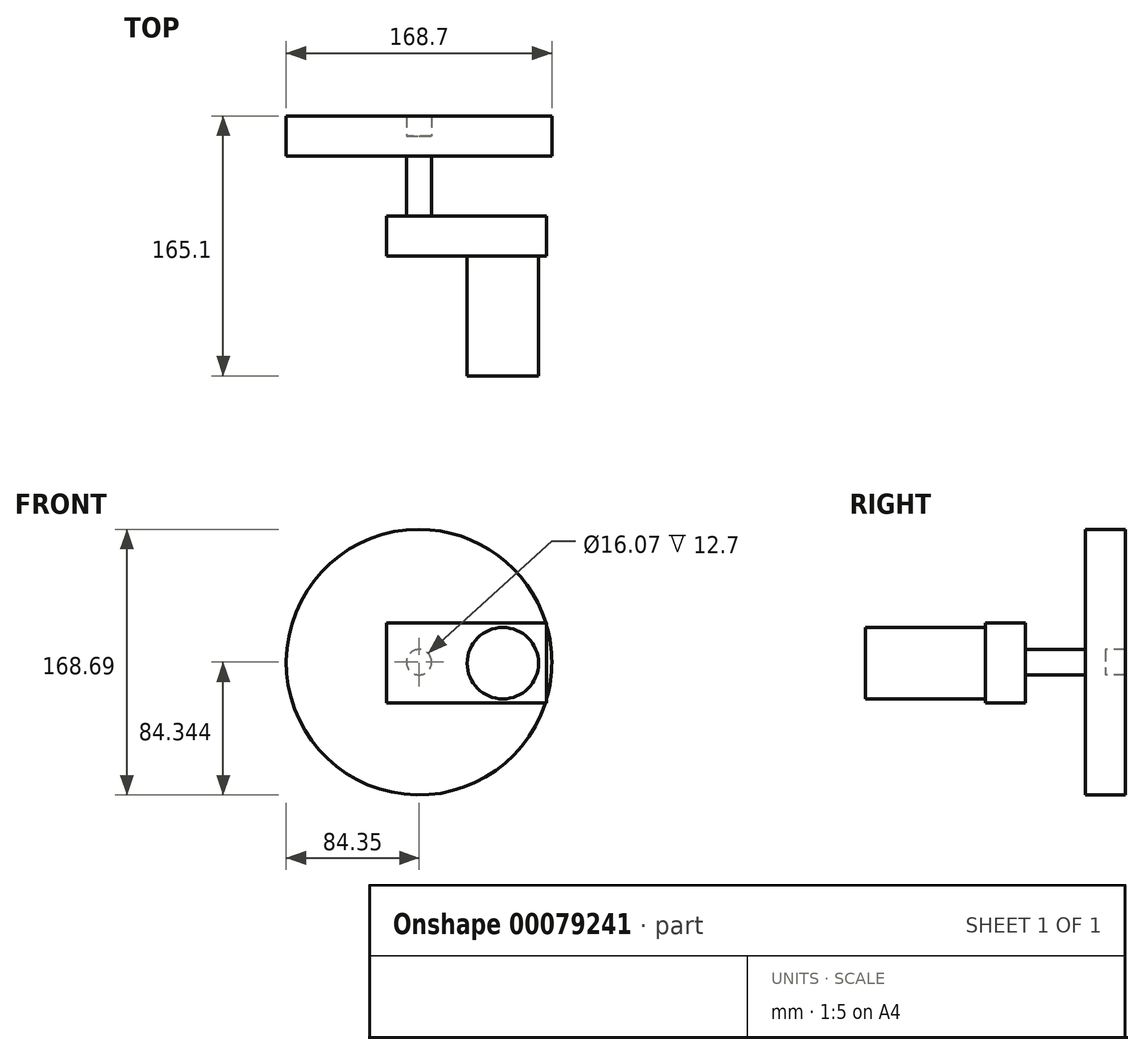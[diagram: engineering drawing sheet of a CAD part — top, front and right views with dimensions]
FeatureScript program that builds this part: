
annotation { "Feature Type Name" : "Feature", "Feature Type Description" : "" }
export const myFeature = defineFeature(function(context is Context, id is Id, definition is map)
    precondition{}
    {
        {
            var Q0;
            Q0=qCreatedBy(makeId("Front.planeOp"),FACE);
            var sketch = newSketch(context, id + "F0", { "sketchPlane" : qUnion([Q0])});
            skLineSegment(sketch, "E0.bottom", {"start": v(0, 0) * mm, "end": v(101.6, 0) * mm});
            skLineSegment(sketch, "E0.top", {"start": v(0, 50.8) * mm, "end": v(101.6, 50.8) * mm});
            skLineSegment(sketch, "E0.left", {"start": v(0, 0) * mm, "end": v(0, 50.8) * mm});
            skLineSegment(sketch, "E0.right", {"start": v(101.6, 0) * mm, "end": v(101.6, 50.8) * mm});
            skSolve(sketch);
        }
        {
            var Q0;
            Q0=makeQuery(id+"F0.imprint","IMPRINT",FACE,{"disambiguationData":[TD([[makeQuery(id+"F0.imprint","IMPRINT",EDGE,{"derivedFrom":sQuery(id+"F0.wireOp",EDGE,"E0.bottom")}),1.0]])]});
            extrude(context, id + "F1", {"entities" : qUnion([Q0]), "depth" : 25.4 * mm});
        }
        {
            var Q0;
            Q0=makeQuery(id+"F1.opExtrude","CAP_FACE",FACE,{"disambiguationData":[OSD([sQuery(id+"F0.wireOp",EDGE,"E0.bottom"),sQuery(id+"F0.wireOp",EDGE,"E0.top"),sQuery(id+"F0.wireOp",EDGE,"E0.left"),sQuery(id+"F0.wireOp",EDGE,"E0.right")])],"isStart":false});
            var sketch = newSketch(context, id + "F2", { "sketchPlane" : qUnion([Q0])});
            skCircle(sketch, "E1", {"center": v(73.72, 25.16) * mm, "radius": 22.67 * mm});
            skSolve(sketch);
        }
        {
            var Q0;
            Q0=makeQuery(id+"F2.imprint","IMPRINT",FACE,{"disambiguationData":[TD([[makeQuery(id+"F2.imprint","IMPRINT",EDGE,{"derivedFrom":sQuery(id+"F2.wireOp",EDGE,"E1")}),1.0]])]});
            extrude(context, id + "F3", {"entities" : qUnion([Q0]), "operationType" : NewBodyOperationType.ADD, "depth" : 76.2 * mm});
        }
        {
            var Q0;
            Q0=makeQuery(id+"F1.opExtrude","CAP_FACE",FACE,{"disambiguationData":[OSD([sQuery(id+"F0.wireOp",EDGE,"E0.bottom"),sQuery(id+"F0.wireOp",EDGE,"E0.top"),sQuery(id+"F0.wireOp",EDGE,"E0.left"),sQuery(id+"F0.wireOp",EDGE,"E0.right")])],"isStart":true});
            var sketch = newSketch(context, id + "F4", { "sketchPlane" : qUnion([Q0])});
            skCircle(sketch, "E2", {"center": v(-20.5, 25.8) * mm, "radius": 8.04 * mm});
            skSolve(sketch);
        }
        {
            var Q0;
            Q0=makeQuery(id+"F4.imprint","IMPRINT",FACE,{"disambiguationData":[TD([[makeQuery(id+"F4.imprint","IMPRINT",EDGE,{"derivedFrom":sQuery(id+"F4.wireOp",EDGE,"E2")}),1.0]])]});
            extrude(context, id + "F5", {"entities" : qUnion([Q0]), "operationType" : NewBodyOperationType.ADD, "depth" : 50.8 * mm});
        }
        {
            var Q0;
            Q0=makeQuery(id+"F5.opExtrude","CAP_FACE",FACE,{"disambiguationData":[OSD([sQuery(id+"F4.wireOp",EDGE,"E2")])],"isStart":false});
            var sketch = newSketch(context, id + "F6", { "sketchPlane" : qUnion([Q0])});
            skCircle(sketch, "E3", {"center": v(-20.5, 25.8) * mm, "radius": 84.35 * mm});
            skSolve(sketch);
        }
        {
            var Q0;
            Q0=makeQuery(id+"F6.imprint","IMPRINT",FACE,{"disambiguationData":[TD([[makeQuery(id+"F6.imprint","IMPRINT",EDGE,{"derivedFrom":sQuery(id+"F6.wireOp",EDGE,"E3")}),1.0]])]});
            extrude(context, id + "F7", {"entities" : qUnion([Q0]), "operationType" : NewBodyOperationType.ADD, "endBound" : BoundingType.SYMMETRIC, "depth" : 25.4 * mm});
        }
    });
